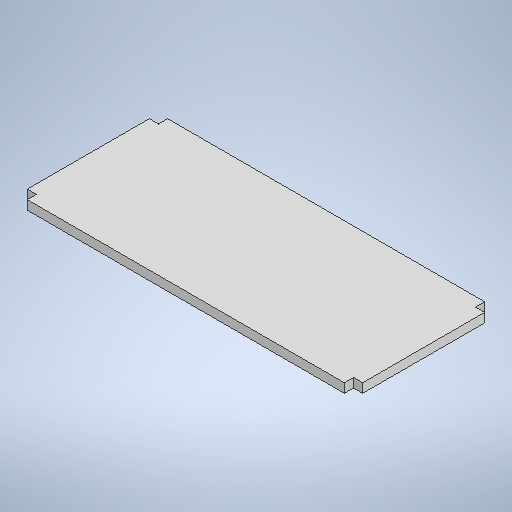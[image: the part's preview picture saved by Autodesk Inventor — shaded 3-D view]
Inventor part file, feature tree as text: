
AUTODESK INVENTOR PART (.ipt)
format: ipt  version: 2025 (Build 290162000, 162)  size: 239,104 bytes
history: native  units: in
note: dims shown in document units (in); Inventor stores cm internally (conversion verified against a paired STEP export)
features: extrude x2, sketch x2
ambient origin geometry x8: Origin, YZ Plane, XZ Plane, XY Plane, X Axis, Y Axis, Z Axis, Center Point
bodies: Solid1 (feature_tree)
feature tree (4):
  extrude  "Extrusion1"  Depth=18.1102in
  extrude  "Extrusion2"  Depth=1.1811in
  sketch  "Sketch1"  dims[d0=43.3071in d1=18.1102in]
  sketch  "Sketch2"  dims[d2=1.1811in d3=0.0in d6=1.1811in d7=1.1811in d8=1.1811in d9=0.0in]
